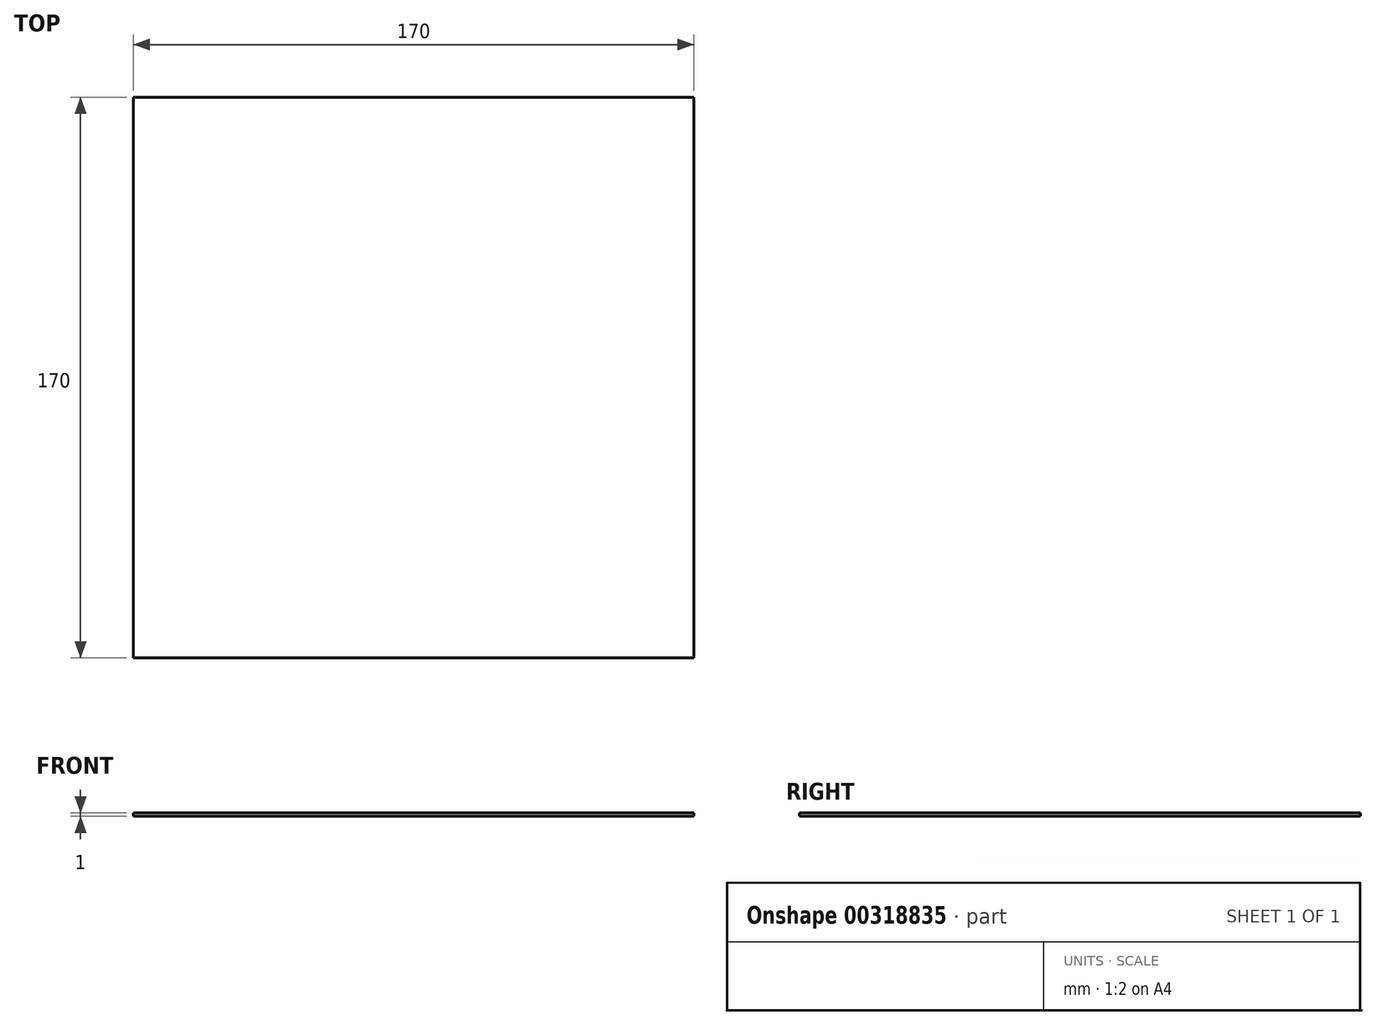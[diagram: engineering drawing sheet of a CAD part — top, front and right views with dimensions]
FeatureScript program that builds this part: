
annotation { "Feature Type Name" : "Feature", "Feature Type Description" : "" }
export const myFeature = defineFeature(function(context is Context, id is Id, definition is map)
    precondition{}
    {
        {
            var Q0;
            Q0=qCreatedBy(makeId("Top.planeOp"),FACE);
            var sketch = newSketch(context, id + "F0", { "sketchPlane" : qUnion([Q0])});
            skLineSegment(sketch, "E0.bottom", {"start": v(-102.4, 128.01) * mm, "end": v(67.6, 128.01) * mm});
            skLineSegment(sketch, "E0.top", {"start": v(-102.4, -41.99) * mm, "end": v(67.6, -41.99) * mm});
            skLineSegment(sketch, "E0.left", {"start": v(-102.4, 128.01) * mm, "end": v(-102.4, -41.99) * mm});
            skLineSegment(sketch, "E0.right", {"start": v(67.6, 128.01) * mm, "end": v(67.6, -41.99) * mm});
            skSolve(sketch);
        }
        {
            var Q0;
            Q0=makeQuery(id+"F0.imprint","IMPRINT",FACE,{"disambiguationData":[TD([[makeQuery(id+"F0.imprint","IMPRINT",EDGE,{"derivedFrom":sQuery(id+"F0.wireOp",EDGE,"E0.bottom")}),-1.0]])]});
            extrude(context, id + "F1", {"entities" : qUnion([Q0]), "depth" : 1 * mm});
        }
    });
